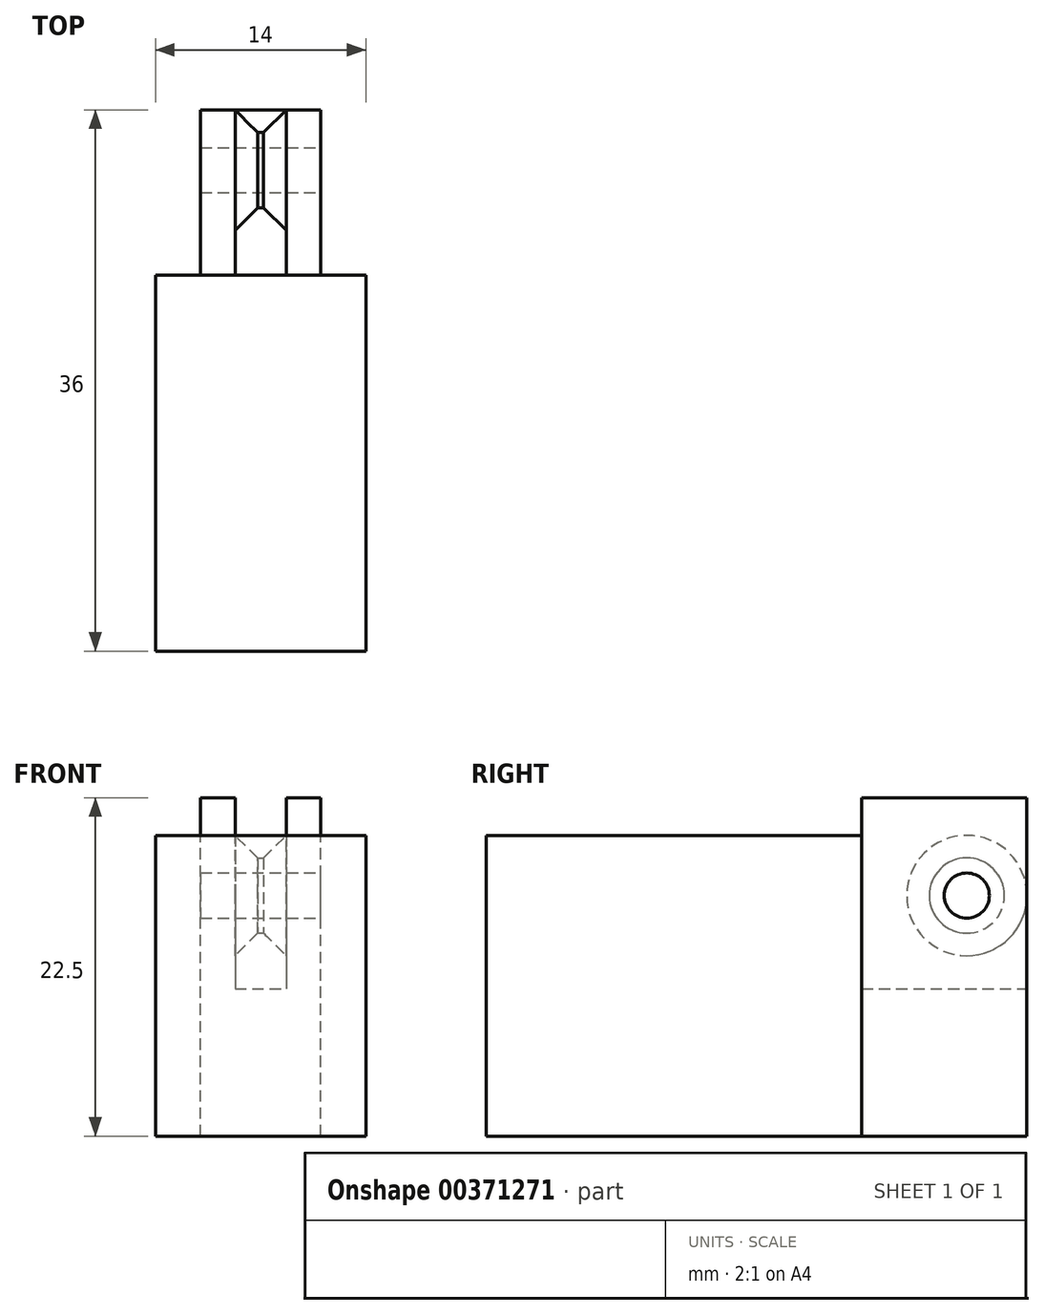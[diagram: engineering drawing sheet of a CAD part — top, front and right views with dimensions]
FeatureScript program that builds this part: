
annotation { "Feature Type Name" : "Feature", "Feature Type Description" : "" }
export const myFeature = defineFeature(function(context is Context, id is Id, definition is map)
    precondition{}
    {
        {
            var Q0;
            Q0=qCreatedBy(makeId("Front.planeOp"),FACE);
            var sketch = newSketch(context, id + "F0", { "sketchPlane" : qUnion([Q0])});
            skLineSegment(sketch, "E0", {"start": v(0, 0) * mm, "end": v(-4, 0) * mm});
            skLineSegment(sketch, "E1", {"start": v(-4, 0) * mm, "end": v(-4, 22.5) * mm});
            skLineSegment(sketch, "E2", {"start": v(-4, 22.5) * mm, "end": v(-1.7, 22.5) * mm});
            skLineSegment(sketch, "E3", {"start": v(-1.7, 22.5) * mm, "end": v(-1.7, 0) * mm, "construction": true});
            skPoint(sketch, "E3.endSnap0", {"position": v(-2, 0) * mm});
            skLineSegment(sketch, "E4", {"start": v(-1.7, 0) * mm, "end": v(-1.7, 9.8) * mm, "construction": true});
            skLineSegment(sketch, "E5", {"start": v(-1.7, 22.5) * mm, "end": v(-1.7, 9.8) * mm});
            skLineSegment(sketch, "E6", {"start": v(-1.7, 9.8) * mm, "end": v(0, 9.8) * mm});
            skLineSegment(sketch, "E7", {"start": v(0, 9.8) * mm, "end": v(0, 0) * mm});
            skSolve(sketch);
        }
        {
            var Q0;
            Q0=makeQuery(id+"F0.imprint","IMPRINT",FACE,{"disambiguationData":[TD([[makeQuery(id+"F0.imprint","IMPRINT",EDGE,{"derivedFrom":sQuery(id+"F0.wireOp",EDGE,"E0")}),-1.0]])]});
            extrude(context, id + "F1", {"entities" : qUnion([Q0]), "depth" : 11 * mm});
        }
        {
            var Q0;
            Q0=makeQuery(id+"F1.opExtrude","SWEPT_BODY",BODY,{"disambiguationData":[OSD([sQuery(id+"F0.wireOp",EDGE,"E0"),sQuery(id+"F0.wireOp",EDGE,"E1"),sQuery(id+"F0.wireOp",EDGE,"E2"),sQuery(id+"F0.wireOp",EDGE,"E5"),sQuery(id+"F0.wireOp",EDGE,"E6"),sQuery(id+"F0.wireOp",EDGE,"E7")])]});
            var Q1;
            Q1=makeQuery(id+"F1.opExtrude","SWEPT_FACE",FACE,{"disambiguationData":[OSD([sQuery(id+"F0.wireOp",EDGE,"E7")])]});
            mirror(context, id + "F2", {"operationType" : NewBodyOperationType.ADD, "entities" : qUnion([Q0]), "mirrorPlane" : qUnion([Q1])});
        }
        {
            var Q0;
            {var subQ0=makeQuery(id+"F1.opExtrude","CAP_FACE",FACE,{"disambiguationData":[OSD([sQuery(id+"F0.wireOp",EDGE,"E0"),sQuery(id+"F0.wireOp",EDGE,"E1"),sQuery(id+"F0.wireOp",EDGE,"E2"),sQuery(id+"F0.wireOp",EDGE,"E5"),sQuery(id+"F0.wireOp",EDGE,"E6"),sQuery(id+"F0.wireOp",EDGE,"E7")])],"isStart":false});Q0=makeQuery(id+"F2.boolean.opBoolean","MERGE",FACE,{"derivedFrom":[subQ0,makeQuery(id+"F2.opPattern","COPY",FACE,{"derivedFrom":subQ0,"instanceName":"1"})]});}
            var sketch = newSketch(context, id + "F3", { "sketchPlane" : qUnion([Q0])});
            skLineSegment(sketch, "E8", {"start": v(0, 0) * mm, "end": v(-7, 0) * mm, "construction": true});
            skLineSegment(sketch, "E9", {"start": v(0, 0) * mm, "end": v(-7, 0) * mm});
            skLineSegment(sketch, "E10", {"start": v(-7, 0) * mm, "end": v(-7, 20) * mm});
            skLineSegment(sketch, "E11", {"start": v(0, 0) * mm, "end": v(7, 0) * mm});
            skLineSegment(sketch, "E12", {"start": v(7, 0) * mm, "end": v(7, 20) * mm});
            skLineSegment(sketch, "E13", {"start": v(-7, 20) * mm, "end": v(7, 20) * mm});
            skSolve(sketch);
        }
        {
            var Q0;
            {var subQ3=sQuery(id+"F3.wireOp",EDGE,"E12");Q0=makeQuery(id+"F3.imprint","IMPRINT",FACE,{"disambiguationData":[TD([[makeQuery(id+"F3.imprint","IMPRINT",EDGE,{"derivedFrom":subQ3}),1.0]])]});}
            var Q1;
            {var subQ13=makeQuery(id+"F1.opExtrude","CAP_EDGE",EDGE,{"disambiguationData":[OSD([sQuery(id+"F0.wireOp",EDGE,"E6")])],"isStart":false});var subQ14=makeQuery(id+"F2.boolean.opBoolean","MERGE",EDGE,{"derivedFrom":[subQ13,makeQuery(id+"F2.opPattern","COPY",EDGE,{"derivedFrom":subQ13,"instanceName":"1"})]});Q1=makeQuery(id+"F3.imprint","IMPRINT",FACE,{"disambiguationData":[TD([[makeQuery(id+"F3.imprint","IMPRINT",EDGE,{"derivedFrom":subQ14}),-1.0]])]});}
            var Q2;
            {var subQ5=makeQuery(id+"F1.opExtrude","CAP_EDGE",EDGE,{"disambiguationData":[OSD([sQuery(id+"F0.wireOp",EDGE,"E6")])],"isStart":false});var subQ6=makeQuery(id+"F2.boolean.opBoolean","MERGE",EDGE,{"derivedFrom":[subQ5,makeQuery(id+"F2.opPattern","COPY",EDGE,{"derivedFrom":subQ5,"instanceName":"1"})]});Q2=makeQuery(id+"F3.imprint","IMPRINT",FACE,{"disambiguationData":[TD([[makeQuery(id+"F3.imprint","IMPRINT",EDGE,{"derivedFrom":subQ6}),1.0]])]});}
            var Q3;
            {var subQ3=sQuery(id+"F3.wireOp",EDGE,"E10");Q3=makeQuery(id+"F3.imprint","IMPRINT",FACE,{"disambiguationData":[TD([[makeQuery(id+"F3.imprint","IMPRINT",EDGE,{"derivedFrom":subQ3}),-1.0]])]});}
            extrude(context, id + "F4", {"entities" : qUnion([Q0, Q1, Q2, Q3]), "operationType" : NewBodyOperationType.ADD, "depth" : 25 * mm});
        }
        {
            var Q0;
            Q0=makeQuery(id+"F2.opPattern","COPY",FACE,{"derivedFrom":makeQuery(id+"F1.opExtrude","SWEPT_FACE",FACE,{"disambiguationData":[OSD([sQuery(id+"F0.wireOp",EDGE,"E1")])]}),"instanceName":"1"});
            var sketch = newSketch(context, id + "F5", { "sketchPlane" : qUnion([Q0])});
            skLineSegment(sketch, "E14", {"start": v(0, 16) * mm, "end": v(-4, 16) * mm, "construction": true});
            skLineSegment(sketch, "E15", {"start": v(-4, 16) * mm, "end": v(-4, 0) * mm, "construction": true});
            skCircle(sketch, "E16", {"center": v(-4, 16) * mm, "radius": 1.5 * mm});
            skCircle(sketch, "E17", {"center": v(-4, 16) * mm, "radius": 2.5 * mm});
            skSolve(sketch);
        }
        {
            var Q0;
            Q0=makeQuery(id+"F5.imprint","IMPRINT",FACE,{"disambiguationData":[TD([[makeQuery(id+"F5.imprint","IMPRINT",EDGE,{"derivedFrom":sQuery(id+"F5.wireOp",EDGE,"E16")}),1.0]])]});
            extrude(context, id + "F6", {"entities" : qUnion([Q0]), "operationType" : NewBodyOperationType.REMOVE, "oppositeDirection" : true, "depth" : 25 * mm});
        }
        {
            var Q0;
            Q0=makeQuery(id+"F5.imprint","IMPRINT",FACE,{"disambiguationData":[TD([[makeQuery(id+"F5.imprint","IMPRINT",EDGE,{"derivedFrom":sQuery(id+"F5.wireOp",EDGE,"E16")}),-1.0]])]});
            var Q1;
            Q1=makeQuery(id+"F1.opExtrude","SWEPT_FACE",FACE,{"disambiguationData":[OSD([sQuery(id+"F0.wireOp",EDGE,"E1")])]});
            extrude(context, id + "F7", {"entities" : qUnion([Q0]), "operationType" : NewBodyOperationType.ADD, "endBound" : BoundingType.UP_TO_SURFACE, "oppositeDirection" : true, "endBoundEntityFace" : qUnion([Q1]), "depth" : 25 * mm});
        }
        {
            var Q0;
            Q0=makeQuery(id+"F7.boolean.opBoolean","INTERSECT",EDGE,{"derivedFrom":[makeQuery(id+"F1.opExtrude","SWEPT_FACE",FACE,{"disambiguationData":[OSD([sQuery(id+"F0.wireOp",EDGE,"E5")])]}),makeQuery(id+"F7.opExtrude","SWEPT_FACE",FACE,{"disambiguationData":[OSD([sQuery(id+"F5.wireOp",EDGE,"E17")])]})]});
            chamfer(context, id + "F8", {"entities" : qUnion([Q0]), "width" : 1.5 * mm, "tangentPropagation" : true});
        }
        {
            var Q0;
            Q0=makeQuery(id+"F7.boolean.opBoolean","INTERSECT",EDGE,{"derivedFrom":[makeQuery(id+"F2.opPattern","COPY",FACE,{"derivedFrom":makeQuery(id+"F1.opExtrude","SWEPT_FACE",FACE,{"disambiguationData":[OSD([sQuery(id+"F0.wireOp",EDGE,"E5")])]}),"instanceName":"1"}),makeQuery(id+"F7.opExtrude","SWEPT_FACE",FACE,{"disambiguationData":[OSD([sQuery(id+"F5.wireOp",EDGE,"E17")])]})]});
            chamfer(context, id + "F9", {"entities" : qUnion([Q0]), "width" : 1.5 * mm, "tangentPropagation" : true});
        }
        {
            var Q0;
            Q0=qCreatedBy(makeId("Front.planeOp"),FACE);
            cPlane(context, id + "F10", {"entities" : qUnion([Q0]), "cplaneType" : CPlaneType.OFFSET, "offset" : 35 * mm, "oppositeDirection" : true, "width" : 150 * mm, "height" : 150 * mm});
        }
    });
